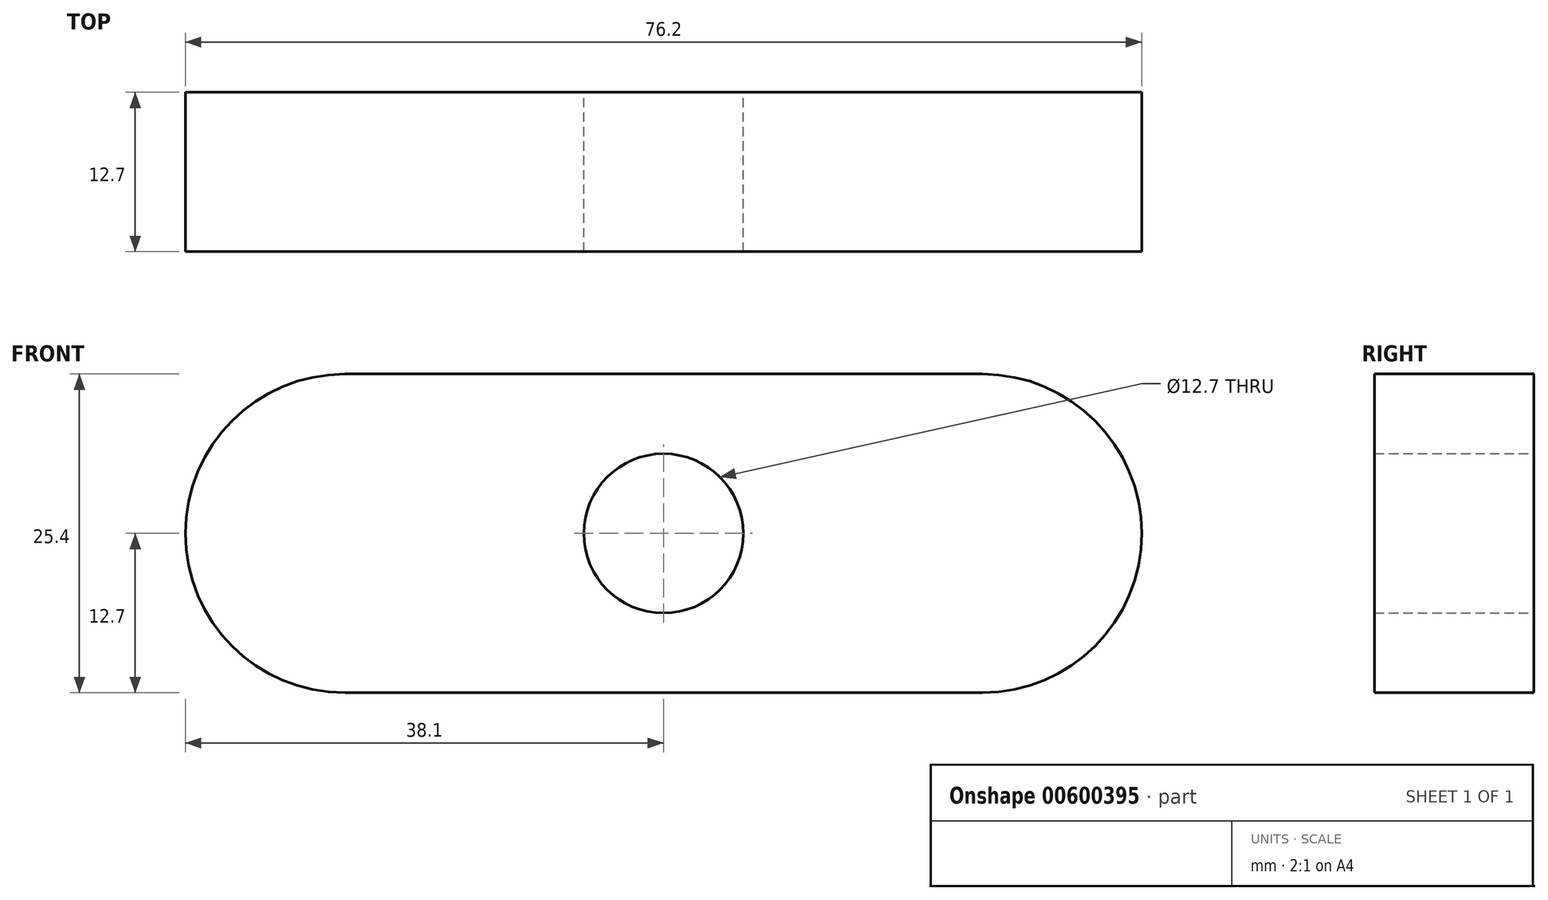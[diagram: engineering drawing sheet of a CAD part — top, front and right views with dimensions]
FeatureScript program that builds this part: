
annotation { "Feature Type Name" : "Feature", "Feature Type Description" : "" }
export const myFeature = defineFeature(function(context is Context, id is Id, definition is map)
    precondition{}
    {
        {
            var Q0;
            Q0=qCreatedBy(makeId("Front.planeOp"),FACE);
            var sketch = newSketch(context, id + "F0", { "sketchPlane" : qUnion([Q0])});
            skLineSegment(sketch, "E0", {"start": v(-25.4, 12.7) * mm, "end": v(25.4, 12.7) * mm});
            skLineSegment(sketch, "E1", {"start": v(25.4, 12.7) * mm, "end": v(25.4, -12.7) * mm, "construction": true});
            skLineSegment(sketch, "E2", {"start": v(25.4, -12.7) * mm, "end": v(-25.4, -12.7) * mm});
            skLineSegment(sketch, "E3", {"start": v(-25.4, -12.7) * mm, "end": v(-25.4, 12.7) * mm, "construction": true});
            skCircle(sketch, "E4", {"center": v(25.4, 0) * mm, "radius": 12.7 * mm});
            skCircle(sketch, "E5", {"center": v(-25.4, 0) * mm, "radius": 12.7 * mm});
            skLineSegment(sketch, "E6", {"start": v(-25.4, 0) * mm, "end": v(25.4, 0) * mm, "construction": true});
            skCircle(sketch, "E7", {"center": v(0, 0) * mm, "radius": 6.35 * mm});
            skSolve(sketch);
        }
        {
            var Q0;
            {var subQ1=sQuery(id+"F0.wireOp",EDGE,"E0");Q0=makeQuery(id+"F0.imprint","IMPRINT",FACE,{"disambiguationData":[TD([[makeQuery(id+"F0.imprint","IMPRINT",EDGE,{"derivedFrom":subQ1}),-1.0]])]});}
            var Q1;
            {var subQ0=sQuery(id+"F0.wireOp",EDGE,"E4");var subQ1=makeQuery(id+"F0.imprint","INTERSECT",VERTEX,{"derivedFrom":[sQuery(id+"F0.wireOp",EDGE,"E0"),subQ0]});Q1=makeQuery(id+"F0.imprint","IMPRINT",FACE,{"disambiguationData":[TD([[makeQuery(id+"F0.imprint","IMPRINT",EDGE,{"disambiguationData":[TD([[subQ1,-1.0]])],"derivedFrom":subQ0}),1.0]])]});}
            var Q2;
            {var subQ0=sQuery(id+"F0.wireOp",EDGE,"E5");var subQ1=makeQuery(id+"F0.imprint","INTERSECT",VERTEX,{"derivedFrom":[sQuery(id+"F0.wireOp",EDGE,"E0"),subQ0]});Q2=makeQuery(id+"F0.imprint","IMPRINT",FACE,{"disambiguationData":[TD([[makeQuery(id+"F0.imprint","IMPRINT",EDGE,{"disambiguationData":[TD([[subQ1,-1.0]])],"derivedFrom":subQ0}),1.0]])]});}
            extrude(context, id + "F1", {"entities" : qUnion([Q0, Q1, Q2]), "endBound" : BoundingType.SYMMETRIC, "depth" : 12.7 * mm, "offsetDistance" : 25.4 * mm});
        }
    });
